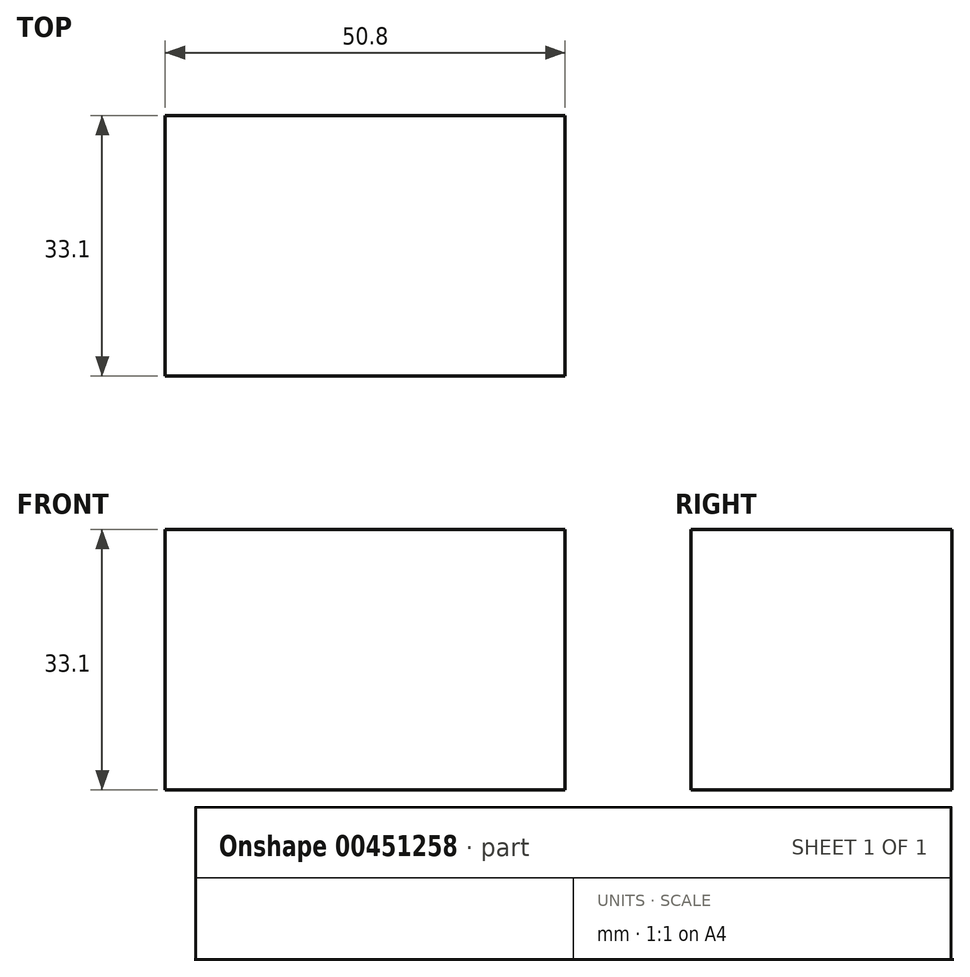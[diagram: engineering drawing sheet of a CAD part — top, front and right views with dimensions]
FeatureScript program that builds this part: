
annotation { "Feature Type Name" : "Feature", "Feature Type Description" : "" }
export const myFeature = defineFeature(function(context is Context, id is Id, definition is map)
    precondition{}
    {
        {
            var Q0;
            Q0=qCreatedBy(makeId("Front.planeOp"),FACE);
            var sketch = newSketch(context, id + "F0", { "sketchPlane" : qUnion([Q0])});
            skLineSegment(sketch, "E0.bottom", {"start": v(25.4, -16.55) * mm, "end": v(-25.4, -16.55) * mm});
            skLineSegment(sketch, "E0.top", {"start": v(25.4, 16.55) * mm, "end": v(-25.4, 16.55) * mm});
            skLineSegment(sketch, "E0.left", {"start": v(25.4, -16.55) * mm, "end": v(25.4, 16.55) * mm});
            skLineSegment(sketch, "E0.right", {"start": v(-25.4, -16.55) * mm, "end": v(-25.4, 16.55) * mm});
            skPoint(sketch, "E0.middle", {"position": v(0, 0) * mm});
            skSolve(sketch);
        }
        {
            var Q0;
            Q0=makeQuery(id+"F0.imprint","IMPRINT",FACE,{"disambiguationData":[TD([[makeQuery(id+"F0.imprint","IMPRINT",EDGE,{"derivedFrom":sQuery(id+"F0.wireOp",EDGE,"E0.bottom")}),-1.0]])]});
            extrude(context, id + "F1", {"entities" : qUnion([Q0]), "depth" : 33.1 * mm});
        }
    });
